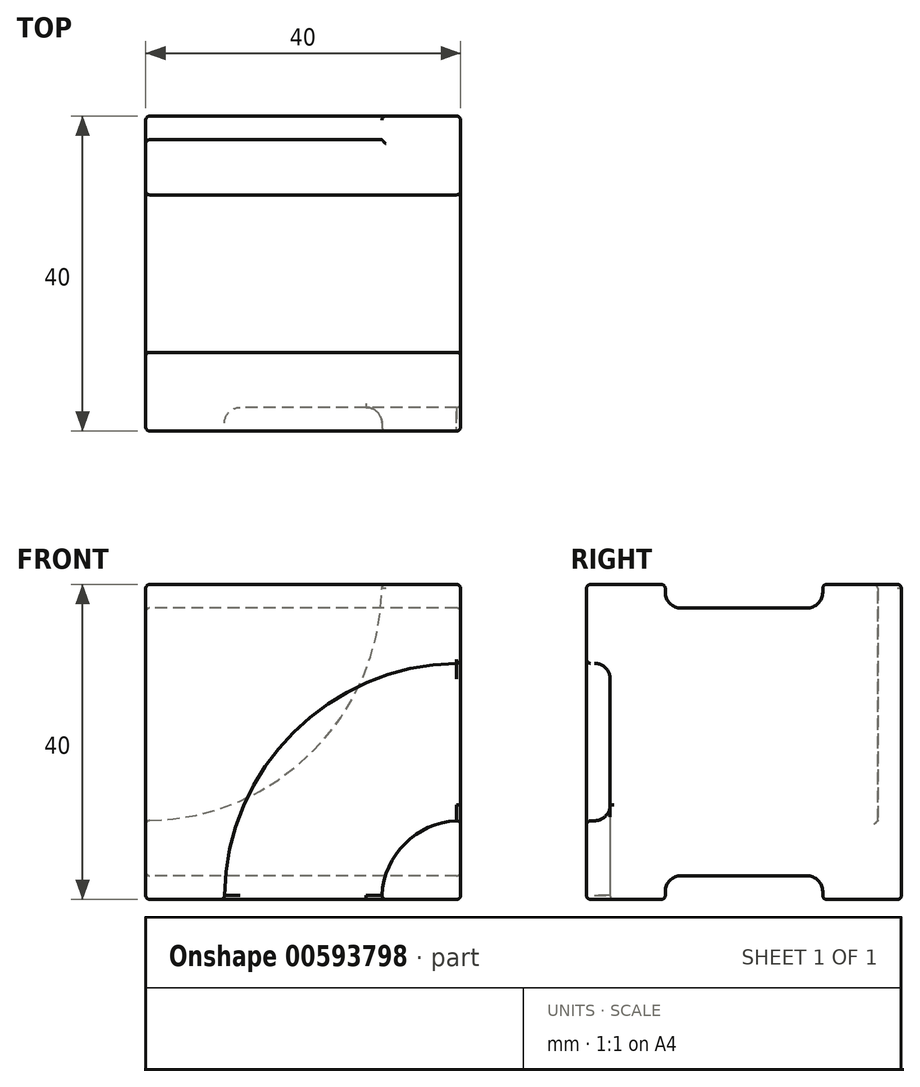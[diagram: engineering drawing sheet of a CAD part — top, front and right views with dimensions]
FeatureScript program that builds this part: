
annotation { "Feature Type Name" : "Feature", "Feature Type Description" : "" }
export const myFeature = defineFeature(function(context is Context, id is Id, definition is map)
    precondition{}
    {
        {
            var Q0;
            Q0=qCreatedBy(makeId("Front.planeOp"),FACE);
            var sketch = newSketch(context, id + "F0", { "sketchPlane" : qUnion([Q0])});
            skLineSegment(sketch, "E0.bottom", {"start": v(20, -20) * mm, "end": v(-20, -20) * mm});
            skLineSegment(sketch, "E0.top", {"start": v(20, 20) * mm, "end": v(-20, 20) * mm});
            skLineSegment(sketch, "E0.left", {"start": v(20, -20) * mm, "end": v(20, 20) * mm});
            skLineSegment(sketch, "E0.right", {"start": v(-20, -20) * mm, "end": v(-20, 20) * mm});
            skPoint(sketch, "E0.middle", {"position": v(0, 0) * mm});
            skSolve(sketch);
        }
        {
            var Q0;
            Q0=makeQuery(id+"F0.imprint","IMPRINT",FACE,{"disambiguationData":[TD([[makeQuery(id+"F0.imprint","IMPRINT",EDGE,{"derivedFrom":sQuery(id+"F0.wireOp",EDGE,"E0.bottom")}),-1.0]])]});
            extrude(context, id + "F1", {"entities" : qUnion([Q0]), "depth" : 40 * mm, "offsetDistance" : 25 * mm, "symmetric" : true});
        }
        {
            var Q0;
            Q0=makeQuery(id+"F1.opExtrude","SWEPT_FACE",FACE,{"disambiguationData":[OSD([sQuery(id+"F0.wireOp",EDGE,"E0.top")])]});
            var sketch = newSketch(context, id + "F2", { "sketchPlane" : qUnion([Q0])});
            skLineSegment(sketch, "E1", {"start": v(34.86, 0) * mm, "end": v(-35.2, 0) * mm, "construction": true});
            skPoint(sketch, "E1.endSnap0", {"position": v(-20, 0) * mm});
            skLineSegment(sketch, "E2.bottom", {"start": v(20, 10) * mm, "end": v(-20, 10) * mm});
            skLineSegment(sketch, "E2.right", {"start": v(-20, 10) * mm, "end": v(-20, 0) * mm});
            skLineSegment(sketch, "E3", {"start": v(20, 10) * mm, "end": v(20, 0) * mm});
            skLineSegment(sketch, "E4.MirrorCS", {"start": v(-20, -10) * mm, "end": v(-20, 0) * mm});
            skLineSegment(sketch, "E5.MirrorCS", {"start": v(20, -10) * mm, "end": v(20, 0) * mm});
            skLineSegment(sketch, "E6.MirrorCS", {"start": v(20, -10) * mm, "end": v(-20, -10) * mm});
            skSolve(sketch);
        }
        {
            var Q0;
            Q0 = qSketchRegion(id + "F2", true);
            extrude(context, id + "F3", {"entities" : qUnion([Q0]), "operationType" : NewBodyOperationType.REMOVE, "oppositeDirection" : true, "depth" : 3 * mm, "offsetDistance" : 25 * mm});
        }
        {
            var Q0;
            Q0=makeQuery(id+"F1.opExtrude","SWEPT_FACE",FACE,{"disambiguationData":[OSD([sQuery(id+"F0.wireOp",EDGE,"E0.bottom")])]});
            var sketch = newSketch(context, id + "F4", { "sketchPlane" : qUnion([Q0])});
            skLineSegment(sketch, "E7", {"start": v(31.12, 0) * mm, "end": v(-32.74, 0) * mm, "construction": true});
            skPoint(sketch, "E7.endSnap0", {"position": v(24.5, 0) * mm});
            skLineSegment(sketch, "E8.bottom", {"start": v(20, 10) * mm, "end": v(-20, 10) * mm});
            skLineSegment(sketch, "E8.top", {"start": v(20, -10) * mm, "end": v(-20, -10) * mm});
            skLineSegment(sketch, "E8.left", {"start": v(20, 10) * mm, "end": v(20, -10) * mm});
            skLineSegment(sketch, "E8.right", {"start": v(-20, 10) * mm, "end": v(-20, -10) * mm});
            skSolve(sketch);
        }
        {
            var Q0;
            Q0 = qSketchRegion(id + "F4", true);
            extrude(context, id + "F5", {"entities" : qUnion([Q0]), "operationType" : NewBodyOperationType.REMOVE, "oppositeDirection" : true, "depth" : 3 * mm, "offsetDistance" : 25 * mm});
        }
        {
            var Q0;
            Q0=makeQuery(id+"F1.opExtrude","CAP_FACE",FACE,{"disambiguationData":[OSD([sQuery(id+"F0.wireOp",EDGE,"E0.bottom"),sQuery(id+"F0.wireOp",EDGE,"E0.top"),sQuery(id+"F0.wireOp",EDGE,"E0.left"),sQuery(id+"F0.wireOp",EDGE,"E0.right")])],"isStart":false});
            var sketch = newSketch(context, id + "F6", { "sketchPlane" : qUnion([Q0])});
            skArc(sketch, "E9", {"start": v(10, -20) * mm, "mid": v(12.93, -12.93) * mm, "end": v(20, -10) * mm});
            skArc(sketch, "E10.0", {"start": v(-10, -20) * mm, "mid": v(-1.21, 1.21) * mm, "end": v(20, 10) * mm});
            skLineSegment(sketch, "E11", {"start": v(10, -20) * mm, "end": v(-10, -20) * mm});
            skLineSegment(sketch, "E12", {"start": v(20, -10) * mm, "end": v(20, 10) * mm});
            skSolve(sketch);
        }
        {
            var Q0;
            Q0 = qSketchRegion(id + "F6", true);
            extrude(context, id + "F7", {"entities" : qUnion([Q0]), "operationType" : NewBodyOperationType.REMOVE, "oppositeDirection" : true, "depth" : 3 * mm, "offsetDistance" : 25 * mm});
        }
        {
            var Q0;
            Q0=makeQuery(id+"F1.opExtrude","CAP_FACE",FACE,{"disambiguationData":[OSD([sQuery(id+"F0.wireOp",EDGE,"E0.bottom"),sQuery(id+"F0.wireOp",EDGE,"E0.top"),sQuery(id+"F0.wireOp",EDGE,"E0.left"),sQuery(id+"F0.wireOp",EDGE,"E0.right")])],"isStart":true});
            var sketch = newSketch(context, id + "F8", { "sketchPlane" : qUnion([Q0])});
            skArc(sketch, "E13", {"start": v(20, 10) * mm, "mid": v(12.93, 12.93) * mm, "end": v(10, 20) * mm});
            skArc(sketch, "E14", {"start": v(20, -10) * mm, "mid": v(-1.21, -1.21) * mm, "end": v(-10, 20) * mm});
            skLineSegment(sketch, "E15", {"start": v(20, -10) * mm, "end": v(20, 10) * mm});
            skLineSegment(sketch, "E16", {"start": v(10, 20) * mm, "end": v(-10, 20) * mm});
            skLineSegment(sketch, "E17", {"start": v(-10, 20) * mm, "end": v(-10, -20) * mm});
            skLineSegment(sketch, "E18", {"start": v(-10, -20) * mm, "end": v(10, -20) * mm});
            skArc(sketch, "E19", {"start": v(10, -20) * mm, "mid": v(12.93, -12.93) * mm, "end": v(20, -10) * mm});
            skSolve(sketch);
        }
        {
            var Q0;
            Q0=makeQuery(id+"F8.imprint","IMPRINT",FACE,{"disambiguationData":[TD([[makeQuery(id+"F8.imprint","IMPRINT",EDGE,{"derivedFrom":sQuery(id+"F8.wireOp",EDGE,"S0vOXXMj-KSPf-uTmC-3DLV-lmScbWxBIAN8")}),1.0]])]});
            var Q1;
            Q1=makeQuery(id+"F8.imprint","IMPRINT",FACE,{"disambiguationData":[TD([[makeQuery(id+"F8.imprint","IMPRINT",EDGE,{"derivedFrom":sQuery(id+"F8.wireOp",EDGE,"E13")}),1.0]])]});
            var Q2;
            Q2=makeQuery(id+"F8.imprint","IMPRINT",FACE,{"disambiguationData":[TD([[makeQuery(id+"F8.imprint","IMPRINT",EDGE,{"derivedFrom":sQuery(id+"F8.wireOp",EDGE,"E14")}),1.0]])]});
            extrude(context, id + "F9", {"entities" : qUnion([Q0, Q1, Q2]), "operationType" : NewBodyOperationType.REMOVE, "oppositeDirection" : true, "depth" : 3 * mm, "offsetDistance" : 25 * mm});
        }
        {
            var Q0;
            Q0=makeQuery(id+"F5.boolean.opBoolean","COPY",EDGE,{"derivedFrom":makeQuery(id+"F5.opExtrude","CAP_EDGE",EDGE,{"disambiguationData":[OSD([sQuery(id+"F4.wireOp",EDGE,"E8.top")])],"isStart":false})});
            var Q1;
            Q1=makeQuery(id+"F5.boolean.opBoolean","COPY",EDGE,{"derivedFrom":makeQuery(id+"F5.opExtrude","CAP_EDGE",EDGE,{"disambiguationData":[OSD([sQuery(id+"F4.wireOp",EDGE,"E8.bottom")])],"isStart":false})});
            var Q2;
            Q2=makeQuery(id+"F7.boolean.opBoolean","COPY",EDGE,{"derivedFrom":makeQuery(id+"F7.opExtrude","CAP_EDGE",EDGE,{"disambiguationData":[OSD([sQuery(id+"F6.wireOp",EDGE,"E10.0")])],"isStart":false})});
            var Q3;
            Q3=makeQuery(id+"F7.boolean.opBoolean","COPY",EDGE,{"derivedFrom":makeQuery(id+"F7.opExtrude","CAP_EDGE",EDGE,{"disambiguationData":[OSD([sQuery(id+"F6.wireOp",EDGE,"E9")])],"isStart":false})});
            var Q4;
            Q4=makeQuery(id+"F9.boolean.opBoolean","COPY",EDGE,{"derivedFrom":makeQuery(id+"F9.opExtrude","CAP_EDGE",EDGE,{"disambiguationData":[OSD([sQuery(id+"F8.wireOp",EDGE,"E17")])],"isStart":false})});
            var Q5;
            Q5=makeQuery(id+"F9.boolean.opBoolean","COPY",EDGE,{"derivedFrom":makeQuery(id+"F9.opExtrude","CAP_EDGE",EDGE,{"disambiguationData":[OSD([sQuery(id+"F8.wireOp",EDGE,"E13")])],"isStart":false})});
            var Q6;
            Q6=makeQuery(id+"F9.boolean.opBoolean","COPY",EDGE,{"derivedFrom":makeQuery(id+"F9.opExtrude","CAP_EDGE",EDGE,{"disambiguationData":[OSD([sQuery(id+"F8.wireOp",EDGE,"E19")])],"isStart":false})});
            var Q7;
            Q7=makeQuery(id+"F3.boolean.opBoolean","COPY",EDGE,{"derivedFrom":makeQuery(id+"F3.opExtrude","CAP_EDGE",EDGE,{"disambiguationData":[OSD([sQuery(id+"F2.wireOp",EDGE,"E6.MirrorCS")])],"isStart":false})});
            var Q8;
            Q8=makeQuery(id+"F3.boolean.opBoolean","COPY",EDGE,{"derivedFrom":makeQuery(id+"F3.opExtrude","CAP_EDGE",EDGE,{"disambiguationData":[OSD([sQuery(id+"F2.wireOp",EDGE,"E2.bottom")])],"isStart":false})});
            fillet(context, id + "F10", {"entities" : qUnion([Q0, Q1, Q2, Q3, Q4, Q5, Q6, Q7, Q8]), "radius" : 2 * mm, "tangentPropagation" : true, "allowEdgeOverflow" : false});
        }
        {
            var Q0;
            {var subQ0=sQuery(id+"F0.wireOp",EDGE,"E0.left");var subQ1=sQuery(id+"F0.wireOp",EDGE,"E0.top");var subQ2=sQuery(id+"F0.wireOp",EDGE,"E0.right");var subQ5=sQuery(id+"F0.wireOp",EDGE,"E0.bottom");Q0=makeQuery(id+"FeEYurADESSjoWS_1.boolean.opBoolean","SPLIT",FACE,{"disambiguationData":[TD([makeQuery(id+"F1.opExtrude","SWEPT_FACE",FACE,{"disambiguationData":[OSD([subQ1])]})])],"derivedFrom":makeQuery(id+"F1.opExtrude","CAP_FACE",FACE,{"disambiguationData":[OSD([subQ5,subQ1,subQ0,subQ2])],"isStart":false})});}
            var Q1;
            Q1=makeQuery(id+"F1.opExtrude","SWEPT_FACE",FACE,{"disambiguationData":[OSD([sQuery(id+"F0.wireOp",EDGE,"E0.right")])]});
            var Q2;
            {var subQ0=sQuery(id+"F0.wireOp",EDGE,"E0.right");var subQ1=sQuery(id+"F0.wireOp",EDGE,"E0.bottom");Q2=makeQuery(id+"FeEYurADESSjoWS_1.boolean.opBoolean","SPLIT",FACE,{"disambiguationData":[TD([makeQuery(id+"FeEYurADESSjoWS_1.opExtrude","SWEPT_FACE",FACE,{"disambiguationData":[OSD([sQuery(id+"F6.wireOp",EDGE,"bcd692f1-bbfa-4d88-a7f8-9c818706eb5d.0")])]})])],"derivedFrom":makeQuery(id+"F1.opExtrude","CAP_FACE",FACE,{"disambiguationData":[OSD([subQ1,sQuery(id+"F0.wireOp",EDGE,"E0.top"),sQuery(id+"F0.wireOp",EDGE,"E0.left"),subQ0])],"isStart":false})});}
            var Q3;
            {var subQ2=sQuery(id+"F0.wireOp",EDGE,"E0.bottom");Q3=makeQuery(id+"F5.boolean.opBoolean","SPLIT",FACE,{"disambiguationData":[TD([makeQuery(id+"F5.opExtrude","SWEPT_FACE",FACE,{"disambiguationData":[OSD([sQuery(id+"F4.wireOp",EDGE,"E8.bottom")])]})])],"derivedFrom":makeQuery(id+"F1.opExtrude","SWEPT_FACE",FACE,{"disambiguationData":[OSD([subQ2])]})});}
            var Q4;
            {var subQ2=sQuery(id+"F0.wireOp",EDGE,"E0.bottom");Q4=makeQuery(id+"F5.boolean.opBoolean","SPLIT",FACE,{"disambiguationData":[TD([makeQuery(id+"F5.opExtrude","SWEPT_FACE",FACE,{"disambiguationData":[OSD([sQuery(id+"F4.wireOp",EDGE,"E8.top")])]})])],"derivedFrom":makeQuery(id+"F1.opExtrude","SWEPT_FACE",FACE,{"disambiguationData":[OSD([subQ2])]})});}
            var Q5;
            {var subQ0=sQuery(id+"F0.wireOp",EDGE,"E0.left");var subQ1=sQuery(id+"F0.wireOp",EDGE,"E0.top");var subQ2=sQuery(id+"F0.wireOp",EDGE,"E0.right");var subQ5=sQuery(id+"F0.wireOp",EDGE,"E0.bottom");Q5=makeQuery(id+"FHPeFrndoI6grQq_1.boolean.opBoolean","SPLIT",FACE,{"disambiguationData":[TD([makeQuery(id+"F1.opExtrude","SWEPT_FACE",FACE,{"disambiguationData":[OSD([subQ1])]})])],"derivedFrom":makeQuery(id+"F1.opExtrude","CAP_FACE",FACE,{"disambiguationData":[OSD([subQ5,subQ1,subQ0,subQ2])],"isStart":true})});}
            var Q6;
            {var subQ0=sQuery(id+"F0.wireOp",EDGE,"E0.left");var subQ1=sQuery(id+"F0.wireOp",EDGE,"E0.bottom");Q6=makeQuery(id+"FHPeFrndoI6grQq_1.boolean.opBoolean","SPLIT",FACE,{"disambiguationData":[TD([makeQuery(id+"FHPeFrndoI6grQq_1.opExtrude","SWEPT_FACE",FACE,{"disambiguationData":[OSD([sQuery(id+"FpqyqDqQfxwQ36t_1.wireOp",EDGE,"11a5f918-374d-4318-88e4-5ad5a2d605e7.0")])]})])],"derivedFrom":makeQuery(id+"F1.opExtrude","CAP_FACE",FACE,{"disambiguationData":[OSD([subQ1,sQuery(id+"F0.wireOp",EDGE,"E0.top"),subQ0,sQuery(id+"F0.wireOp",EDGE,"E0.right")])],"isStart":true})});}
            var Q7;
            {var subQ0=sQuery(id+"F0.wireOp",EDGE,"E0.left");Q7=makeQuery(id+"FhphGXGLthVadN0_1.boolean.opBoolean","SPLIT",FACE,{"disambiguationData":[TD([makeQuery(id+"F5.boolean.opBoolean","COPY",FACE,{"derivedFrom":makeQuery(id+"F5.opExtrude","SWEPT_FACE",FACE,{"disambiguationData":[OSD([sQuery(id+"F4.wireOp",EDGE,"E8.top")])]})})])],"derivedFrom":makeQuery(id+"F1.opExtrude","SWEPT_FACE",FACE,{"disambiguationData":[OSD([subQ0])]})});}
            var Q8;
            {var subQ0=sQuery(id+"F0.wireOp",EDGE,"E0.top");var subQ2=sQuery(id+"F0.wireOp",EDGE,"E0.left");Q8=makeQuery(id+"FhphGXGLthVadN0_1.boolean.opBoolean","SPLIT",FACE,{"disambiguationData":[TD([makeQuery(id+"F1.opExtrude","SWEPT_FACE",FACE,{"disambiguationData":[OSD([subQ0])]})])],"derivedFrom":makeQuery(id+"F1.opExtrude","SWEPT_FACE",FACE,{"disambiguationData":[OSD([subQ2])]})});}
            var Q9;
            {var subQ0=sQuery(id+"F0.wireOp",EDGE,"E0.left");Q9=makeQuery(id+"FhphGXGLthVadN0_1.boolean.opBoolean","SPLIT",FACE,{"disambiguationData":[TD([makeQuery(id+"F5.boolean.opBoolean","COPY",FACE,{"derivedFrom":makeQuery(id+"F5.opExtrude","SWEPT_FACE",FACE,{"disambiguationData":[OSD([sQuery(id+"F4.wireOp",EDGE,"E8.bottom")])]})})])],"derivedFrom":makeQuery(id+"F1.opExtrude","SWEPT_FACE",FACE,{"disambiguationData":[OSD([subQ0])]})});}
            var Q10;
            {var subQ1=sQuery(id+"F0.wireOp",EDGE,"E0.left");var subQ2=sQuery(id+"F0.wireOp",EDGE,"E0.top");Q10=makeQuery(id+"F3.boolean.opBoolean","SPLIT",FACE,{"disambiguationData":[TD([makeQuery(id+"F1.opExtrude","SWEPT_FACE",FACE,{"disambiguationData":[OSD([subQ1])]})])],"derivedFrom":makeQuery(id+"F1.opExtrude","SWEPT_FACE",FACE,{"disambiguationData":[OSD([subQ2])]})});}
            var Q11;
            {var subQ0=sQuery(id+"F0.wireOp",EDGE,"E0.right");var subQ2=sQuery(id+"F0.wireOp",EDGE,"E0.top");Q11=makeQuery(id+"F3.boolean.opBoolean","SPLIT",FACE,{"disambiguationData":[TD([makeQuery(id+"F1.opExtrude","SWEPT_FACE",FACE,{"disambiguationData":[OSD([subQ0])]})])],"derivedFrom":makeQuery(id+"F1.opExtrude","SWEPT_FACE",FACE,{"disambiguationData":[OSD([subQ2])]})});}
            var Q12;
            Q12=makeQuery(id+"FhphGXGLthVadN0_1.boolean.opBoolean","COPY",EDGE,{"derivedFrom":makeQuery(id+"FhphGXGLthVadN0_1.opExtrude","CAP_EDGE",EDGE,{"disambiguationData":[OSD([sQuery(id+"F0.wireOp",EDGE,"E0.left"),sQuery(id+"FpqyqDqQfxwQ36t_1.wireOp",EDGE,"0759713e-e7df-4183-9224-c0852353a63a.0"),sQuery(id+"FpqyqDqQfxwQ36t_1.wireOp",EDGE,"0759713e-e7df-4183-9224-c0852353a63a.1"),sQuery(id+"FpqyqDqQfxwQ36t_1.wireOp",EDGE,"11a5f918-374d-4318-88e4-5ad5a2d605e7.0"),sQuery(id+"FpqyqDqQfxwQ36t_1.wireOp",EDGE,"11a5f918-374d-4318-88e4-5ad5a2d605e7.1"),sQuery(id+"FpqyqDqQfxwQ36t_1.wireOp",EDGE,"zKdxWZJF-1CZ5-eTvP-v24i-ATzPNmKQrU5U"),sQuery(id+"FpqyqDqQfxwQ36t_1.wireOp",EDGE,"wMGJVRBH-eHaP-nP1o-tBN4-yRPVe8nUY65C"),sQuery(id+"FpqyqDqQfxwQ36t_1.wireOp",EDGE,"61521492-cf4c-4c9f-b70c-34a3293a7591.filletArc"),sQuery(id+"FpqyqDqQfxwQ36t_1.wireOp",EDGE,"dc6e6eda-5071-4c0c-bfe8-26dd1b046b33.filletArc")])],"isStart":false})});
            var Q13;
            Q13=makeQuery(id+"FhphGXGLthVadN0_1.boolean.opBoolean","COPY",EDGE,{"derivedFrom":makeQuery(id+"FhphGXGLthVadN0_1.opExtrude","CAP_EDGE",EDGE,{"disambiguationData":[OSD([sQuery(id+"FWu8rZYhLeN4OZv_1.wireOp",EDGE,"ZuCWKp1C-7wbl-hlMd-doiS-uhh4Hec1rI5d")])],"isStart":false})});
            fillet(context, id + "F11", {"entities" : qUnion([Q0, Q1, Q2, Q3, Q4, Q5, Q6, Q7, Q8, Q9, Q10, Q11, Q12, Q13]), "radius" : 0.5 * mm, "tangentPropagation" : true, "allowEdgeOverflow" : false});
        }
    });
